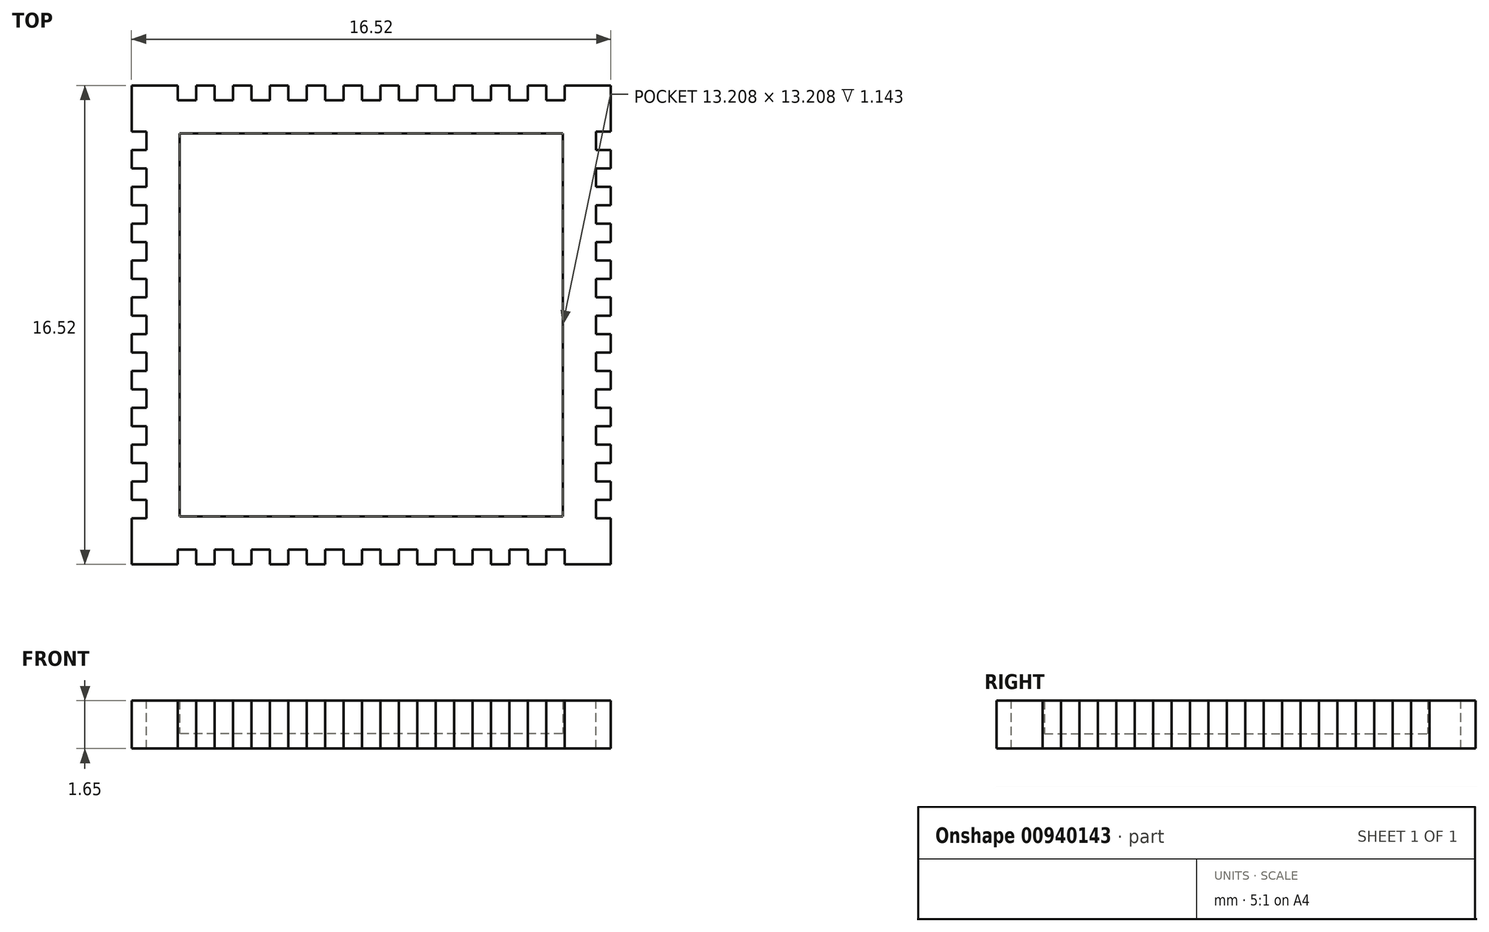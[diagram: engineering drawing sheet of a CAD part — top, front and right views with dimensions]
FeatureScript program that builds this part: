
annotation { "Feature Type Name" : "Feature", "Feature Type Description" : "" }
export const myFeature = defineFeature(function(context is Context, id is Id, definition is map)
    precondition{}
    {
        {
            var Q0;
            Q0=qCreatedBy(makeId("Top.planeOp"),FACE);
            var sketch = newSketch(context, id + "F0", { "sketchPlane" : qUnion([Q0])});
            skLineSegment(sketch, "E0.bottom", {"start": v(8.26, -8.26) * mm, "end": v(-8.26, -8.26) * mm});
            skLineSegment(sketch, "E0.top", {"start": v(8.26, 8.26) * mm, "end": v(-8.26, 8.26) * mm});
            skLineSegment(sketch, "E0.left", {"start": v(8.26, -8.26) * mm, "end": v(8.26, 8.26) * mm});
            skLineSegment(sketch, "E0.right", {"start": v(-8.26, -8.26) * mm, "end": v(-8.26, 8.26) * mm});
            skPoint(sketch, "E0.middle", {"position": v(0, 0) * mm});
            skLineSegment(sketch, "E1.bottom", {"start": v(6.6, -6.6) * mm, "end": v(-6.6, -6.6) * mm});
            skLineSegment(sketch, "E1.top", {"start": v(6.6, 6.6) * mm, "end": v(-6.6, 6.6) * mm});
            skLineSegment(sketch, "E1.left", {"start": v(6.6, -6.6) * mm, "end": v(6.6, 6.6) * mm});
            skLineSegment(sketch, "E1.right", {"start": v(-6.6, -6.6) * mm, "end": v(-6.6, 6.6) * mm});
            skSolve(sketch);
        }
        {
            var Q0;
            Q0=makeQuery(id+"F0.imprint","IMPRINT",FACE,{"disambiguationData":[TD([[makeQuery(id+"F0.imprint","IMPRINT",EDGE,{"derivedFrom":sQuery(id+"F0.wireOp",EDGE,"E1.bottom")}),-1.0]])]});
            extrude(context, id + "F1", {"entities" : qUnion([Q0]), "depth" : 0.5 * mm, "offsetDistance" : 25 * mm});
        }
        {
            var Q0;
            Q0=makeQuery(id+"F0.imprint","IMPRINT",FACE,{"disambiguationData":[TD([[makeQuery(id+"F0.imprint","IMPRINT",EDGE,{"derivedFrom":sQuery(id+"F0.wireOp",EDGE,"E0.bottom")}),-1.0]])]});
            extrude(context, id + "F2", {"entities" : qUnion([Q0]), "operationType" : NewBodyOperationType.ADD, "depth" : 1.65 * mm, "offsetDistance" : 25 * mm});
        }
        {
            var Q0;
            Q0=makeQuery(id+"F2.opExtrude","SWEPT_FACE",FACE,{"disambiguationData":[OSD([sQuery(id+"F0.wireOp",EDGE,"E0.bottom")])]});
            var sketch = newSketch(context, id + "F3", { "sketchPlane" : qUnion([Q0])});
            skLineSegment(sketch, "E2.bottom", {"start": v(-6.03, 0) * mm, "end": v(-6.67, 0) * mm});
            skLineSegment(sketch, "E2.top", {"start": v(-6.03, 1.65) * mm, "end": v(-6.67, 1.65) * mm});
            skLineSegment(sketch, "E2.left", {"start": v(-6.03, 0) * mm, "end": v(-6.03, 1.65) * mm});
            skLineSegment(sketch, "E2.right", {"start": v(-6.67, 0) * mm, "end": v(-6.67, 1.65) * mm});
            skPoint(sketch, "E2.middle", {"position": v(-6.35, 0.83) * mm});
            skLineSegment(sketch, "E3.bottom", {"start": v(-4.76, 0) * mm, "end": v(-5.4, 0) * mm});
            skLineSegment(sketch, "E3.top", {"start": v(-4.76, 1.65) * mm, "end": v(-5.4, 1.65) * mm});
            skLineSegment(sketch, "E3.left", {"start": v(-4.76, 0) * mm, "end": v(-4.76, 1.65) * mm});
            skLineSegment(sketch, "E3.right", {"start": v(-5.4, 0) * mm, "end": v(-5.4, 1.65) * mm});
            skPoint(sketch, "E3.middle", {"position": v(-5.08, 0.83) * mm});
            skLineSegment(sketch, "E4.MirrorCS", {"start": v(-4.13, 0) * mm, "end": v(-3.5, 0) * mm});
            skLineSegment(sketch, "E5.MirrorCS", {"start": v(-4.13, 1.65) * mm, "end": v(-3.5, 1.65) * mm});
            skPoint(sketch, "E6.MirrorP", {"position": v(-2.8, 0.8) * mm});
            skLineSegment(sketch, "E7.MirrorCS", {"start": v(-4.13, 0) * mm, "end": v(-4.13, 1.65) * mm});
            skLineSegment(sketch, "E8.MirrorCS", {"start": v(-2.86, 0) * mm, "end": v(-2.22, 0) * mm});
            skLineSegment(sketch, "E9.MirrorCS", {"start": v(-2.22, 0) * mm, "end": v(-2.22, 1.65) * mm});
            skLineSegment(sketch, "E10.MirrorCS", {"start": v(-2.86, 0) * mm, "end": v(-2.86, 1.65) * mm});
            skPoint(sketch, "E11.MirrorP", {"position": v(-4.1, 0.84) * mm});
            skLineSegment(sketch, "E12.MirrorCS", {"start": v(-3.5, 0) * mm, "end": v(-3.5, 1.65) * mm});
            skLineSegment(sketch, "E13.MirrorCS", {"start": v(-2.86, 1.65) * mm, "end": v(-2.22, 1.65) * mm});
            skLineSegment(sketch, "E14.MirrorCS", {"start": v(0.32, 0) * mm, "end": v(-0.32, 0) * mm});
            skPoint(sketch, "E15.MirrorP", {"position": v(-0.3, 0.84) * mm});
            skLineSegment(sketch, "E16.MirrorCS", {"start": v(-1.59, 0) * mm, "end": v(-1.59, 1.65) * mm});
            skLineSegment(sketch, "E17.MirrorCS", {"start": v(0.95, 0) * mm, "end": v(0.95, 1.65) * mm});
            skLineSegment(sketch, "E18.MirrorCS", {"start": v(-0.32, 0) * mm, "end": v(-0.32, 1.65) * mm});
            skLineSegment(sketch, "E19.MirrorCS", {"start": v(0.32, 0) * mm, "end": v(0.32, 1.65) * mm});
            skPoint(sketch, "E20.MirrorP", {"position": v(-1.56, 0.82) * mm});
            skLineSegment(sketch, "E21.MirrorCS", {"start": v(2.22, 1.65) * mm, "end": v(2.86, 1.65) * mm});
            skLineSegment(sketch, "E22.MirrorCS", {"start": v(2.86, 0) * mm, "end": v(2.86, 1.65) * mm});
            skLineSegment(sketch, "E23.MirrorCS", {"start": v(-0.95, 1.65) * mm, "end": v(-1.59, 1.65) * mm});
            skPoint(sketch, "E24.MirrorP", {"position": v(2.22, 0.83) * mm});
            skLineSegment(sketch, "E25.MirrorCS", {"start": v(-0.95, 0) * mm, "end": v(-1.59, 0) * mm});
            skLineSegment(sketch, "E26.MirrorCS", {"start": v(-0.95, 0) * mm, "end": v(-0.95, 1.65) * mm});
            skLineSegment(sketch, "E27.MirrorCS", {"start": v(0.95, 0) * mm, "end": v(1.59, 0) * mm});
            skLineSegment(sketch, "E28.MirrorCS", {"start": v(0.32, 1.65) * mm, "end": v(-0.32, 1.65) * mm});
            skLineSegment(sketch, "E29.MirrorCS", {"start": v(1.59, 0) * mm, "end": v(1.59, 1.65) * mm});
            skLineSegment(sketch, "E30.MirrorCS", {"start": v(0.95, 1.65) * mm, "end": v(1.59, 1.65) * mm});
            skLineSegment(sketch, "E31.MirrorCS", {"start": v(2.22, 0) * mm, "end": v(2.22, 1.65) * mm});
            skLineSegment(sketch, "E32.MirrorCS", {"start": v(2.22, 0) * mm, "end": v(2.86, 0) * mm});
            skPoint(sketch, "E33.MirrorP", {"position": v(0.95, 0.83) * mm});
            skLineSegment(sketch, "E34.MirrorCS", {"start": v(3.5, 0) * mm, "end": v(3.5, 1.65) * mm});
            skPoint(sketch, "E35.MirrorP", {"position": v(5.96, 0.82) * mm});
            skLineSegment(sketch, "E36.MirrorCS", {"start": v(6.03, 0) * mm, "end": v(6.67, 0) * mm});
            skLineSegment(sketch, "E37.MirrorCS", {"start": v(6.03, 0) * mm, "end": v(6.03, 1.65) * mm});
            skLineSegment(sketch, "E38.MirrorCS", {"start": v(5.4, 1.65) * mm, "end": v(4.76, 1.65) * mm});
            skPoint(sketch, "E39.MirrorP", {"position": v(4.76, 0.83) * mm});
            skLineSegment(sketch, "E40.MirrorCS", {"start": v(6.67, 0) * mm, "end": v(6.67, 1.65) * mm});
            skLineSegment(sketch, "E41.MirrorCS", {"start": v(5.4, 0) * mm, "end": v(5.4, 1.65) * mm});
            skLineSegment(sketch, "E42.MirrorCS", {"start": v(4.13, 0) * mm, "end": v(4.13, 1.65) * mm});
            skLineSegment(sketch, "E43.MirrorCS", {"start": v(4.76, 0) * mm, "end": v(4.76, 1.65) * mm});
            skLineSegment(sketch, "E44.MirrorCS", {"start": v(4.13, 0) * mm, "end": v(3.5, 0) * mm});
            skLineSegment(sketch, "E45.MirrorCS", {"start": v(5.4, 0) * mm, "end": v(4.76, 0) * mm});
            skLineSegment(sketch, "E46.MirrorCS", {"start": v(6.03, 1.65) * mm, "end": v(6.67, 1.65) * mm});
            skPoint(sketch, "E47.MirrorP", {"position": v(3.5, 0.83) * mm});
            skLineSegment(sketch, "E48.MirrorCS", {"start": v(4.13, 1.65) * mm, "end": v(3.5, 1.65) * mm});
            skLineSegment(sketch, "E49", {"start": v(-8.26, 0.83) * mm, "end": v(8.26, 0.83) * mm});
            skSolve(sketch);
        }
        {
            var Q0;
            {var subQ0=sQuery(id+"F3.wireOp",EDGE,"E2.top");Q0=makeQuery(id+"F3.imprint","IMPRINT",FACE,{"disambiguationData":[TD([[makeQuery(id+"F3.imprint","IMPRINT",EDGE,{"derivedFrom":subQ0}),1.0]])]});}
            var Q1;
            {var subQ0=sQuery(id+"F3.wireOp",EDGE,"E2.bottom");Q1=makeQuery(id+"F3.imprint","IMPRINT",FACE,{"disambiguationData":[TD([[makeQuery(id+"F3.imprint","IMPRINT",EDGE,{"derivedFrom":subQ0}),-1.0]])]});}
            var Q2;
            {var subQ0=sQuery(id+"F3.wireOp",EDGE,"E3.top");Q2=makeQuery(id+"F3.imprint","IMPRINT",FACE,{"disambiguationData":[TD([[makeQuery(id+"F3.imprint","IMPRINT",EDGE,{"derivedFrom":subQ0}),1.0]])]});}
            var Q3;
            {var subQ0=sQuery(id+"F3.wireOp",EDGE,"E3.bottom");Q3=makeQuery(id+"F3.imprint","IMPRINT",FACE,{"disambiguationData":[TD([[makeQuery(id+"F3.imprint","IMPRINT",EDGE,{"derivedFrom":subQ0}),-1.0]])]});}
            var Q4;
            {var subQ0=sQuery(id+"F3.wireOp",EDGE,"E5.MirrorCS");Q4=makeQuery(id+"F3.imprint","IMPRINT",FACE,{"disambiguationData":[TD([[makeQuery(id+"F3.imprint","IMPRINT",EDGE,{"derivedFrom":subQ0}),1.0]])]});}
            var Q5;
            {var subQ0=sQuery(id+"F3.wireOp",EDGE,"E4.MirrorCS");Q5=makeQuery(id+"F3.imprint","IMPRINT",FACE,{"disambiguationData":[TD([[makeQuery(id+"F3.imprint","IMPRINT",EDGE,{"derivedFrom":subQ0}),-1.0]])]});}
            var Q6;
            {var subQ0=sQuery(id+"F3.wireOp",EDGE,"E13.MirrorCS");Q6=makeQuery(id+"F3.imprint","IMPRINT",FACE,{"disambiguationData":[TD([[makeQuery(id+"F3.imprint","IMPRINT",EDGE,{"derivedFrom":subQ0}),1.0]])]});}
            var Q7;
            {var subQ0=sQuery(id+"F3.wireOp",EDGE,"E8.MirrorCS");Q7=makeQuery(id+"F3.imprint","IMPRINT",FACE,{"disambiguationData":[TD([[makeQuery(id+"F3.imprint","IMPRINT",EDGE,{"derivedFrom":subQ0}),-1.0]])]});}
            var Q8;
            {var subQ0=sQuery(id+"F3.wireOp",EDGE,"E23.MirrorCS");Q8=makeQuery(id+"F3.imprint","IMPRINT",FACE,{"disambiguationData":[TD([[makeQuery(id+"F3.imprint","IMPRINT",EDGE,{"derivedFrom":subQ0}),1.0]])]});}
            var Q9;
            {var subQ0=sQuery(id+"F3.wireOp",EDGE,"E25.MirrorCS");Q9=makeQuery(id+"F3.imprint","IMPRINT",FACE,{"disambiguationData":[TD([[makeQuery(id+"F3.imprint","IMPRINT",EDGE,{"derivedFrom":subQ0}),-1.0]])]});}
            var Q10;
            {var subQ0=sQuery(id+"F3.wireOp",EDGE,"E28.MirrorCS");Q10=makeQuery(id+"F3.imprint","IMPRINT",FACE,{"disambiguationData":[TD([[makeQuery(id+"F3.imprint","IMPRINT",EDGE,{"derivedFrom":subQ0}),1.0]])]});}
            var Q11;
            {var subQ0=sQuery(id+"F3.wireOp",EDGE,"E14.MirrorCS");Q11=makeQuery(id+"F3.imprint","IMPRINT",FACE,{"disambiguationData":[TD([[makeQuery(id+"F3.imprint","IMPRINT",EDGE,{"derivedFrom":subQ0}),-1.0]])]});}
            var Q12;
            {var subQ0=sQuery(id+"F3.wireOp",EDGE,"E30.MirrorCS");Q12=makeQuery(id+"F3.imprint","IMPRINT",FACE,{"disambiguationData":[TD([[makeQuery(id+"F3.imprint","IMPRINT",EDGE,{"derivedFrom":subQ0}),1.0]])]});}
            var Q13;
            {var subQ0=sQuery(id+"F3.wireOp",EDGE,"E27.MirrorCS");Q13=makeQuery(id+"F3.imprint","IMPRINT",FACE,{"disambiguationData":[TD([[makeQuery(id+"F3.imprint","IMPRINT",EDGE,{"derivedFrom":subQ0}),-1.0]])]});}
            var Q14;
            {var subQ0=sQuery(id+"F3.wireOp",EDGE,"E21.MirrorCS");Q14=makeQuery(id+"F3.imprint","IMPRINT",FACE,{"disambiguationData":[TD([[makeQuery(id+"F3.imprint","IMPRINT",EDGE,{"derivedFrom":subQ0}),1.0]])]});}
            var Q15;
            {var subQ0=sQuery(id+"F3.wireOp",EDGE,"E32.MirrorCS");Q15=makeQuery(id+"F3.imprint","IMPRINT",FACE,{"disambiguationData":[TD([[makeQuery(id+"F3.imprint","IMPRINT",EDGE,{"derivedFrom":subQ0}),-1.0]])]});}
            var Q16;
            {var subQ0=sQuery(id+"F3.wireOp",EDGE,"E48.MirrorCS");Q16=makeQuery(id+"F3.imprint","IMPRINT",FACE,{"disambiguationData":[TD([[makeQuery(id+"F3.imprint","IMPRINT",EDGE,{"derivedFrom":subQ0}),1.0]])]});}
            var Q17;
            {var subQ0=sQuery(id+"F3.wireOp",EDGE,"E44.MirrorCS");Q17=makeQuery(id+"F3.imprint","IMPRINT",FACE,{"disambiguationData":[TD([[makeQuery(id+"F3.imprint","IMPRINT",EDGE,{"derivedFrom":subQ0}),-1.0]])]});}
            var Q18;
            {var subQ0=sQuery(id+"F3.wireOp",EDGE,"E38.MirrorCS");Q18=makeQuery(id+"F3.imprint","IMPRINT",FACE,{"disambiguationData":[TD([[makeQuery(id+"F3.imprint","IMPRINT",EDGE,{"derivedFrom":subQ0}),1.0]])]});}
            var Q19;
            {var subQ0=sQuery(id+"F3.wireOp",EDGE,"E45.MirrorCS");Q19=makeQuery(id+"F3.imprint","IMPRINT",FACE,{"disambiguationData":[TD([[makeQuery(id+"F3.imprint","IMPRINT",EDGE,{"derivedFrom":subQ0}),-1.0]])]});}
            var Q20;
            {var subQ0=sQuery(id+"F3.wireOp",EDGE,"E46.MirrorCS");Q20=makeQuery(id+"F3.imprint","IMPRINT",FACE,{"disambiguationData":[TD([[makeQuery(id+"F3.imprint","IMPRINT",EDGE,{"derivedFrom":subQ0}),1.0]])]});}
            var Q21;
            {var subQ0=sQuery(id+"F3.wireOp",EDGE,"E36.MirrorCS");Q21=makeQuery(id+"F3.imprint","IMPRINT",FACE,{"disambiguationData":[TD([[makeQuery(id+"F3.imprint","IMPRINT",EDGE,{"derivedFrom":subQ0}),-1.0]])]});}
            extrude(context, id + "F4", {"entities" : qUnion([Q0, Q1, Q2, Q3, Q4, Q5, Q6, Q7, Q8, Q9, Q10, Q11, Q12, Q13, Q14, Q15, Q16, Q17, Q18, Q19, Q20, Q21]), "operationType" : NewBodyOperationType.REMOVE, "oppositeDirection" : true, "depth" : 0.5 * mm, "offsetDistance" : 25 * mm});
        }
        {
            var Q0;
            Q0=makeQuery(id+"F2.opExtrude","SWEPT_FACE",FACE,{"disambiguationData":[OSD([sQuery(id+"F0.wireOp",EDGE,"E0.left")])]});
            var sketch = newSketch(context, id + "F5", { "sketchPlane" : qUnion([Q0])});
            skLineSegment(sketch, "E50.bottom", {"start": v(-6.03, 0) * mm, "end": v(-6.67, 0) * mm});
            skLineSegment(sketch, "E50.top", {"start": v(-6.03, 1.65) * mm, "end": v(-6.67, 1.65) * mm});
            skLineSegment(sketch, "E50.left", {"start": v(-6.03, 0) * mm, "end": v(-6.03, 1.65) * mm});
            skLineSegment(sketch, "E50.right", {"start": v(-6.67, 0) * mm, "end": v(-6.67, 1.65) * mm});
            skPoint(sketch, "E50.middle", {"position": v(-6.35, 0.83) * mm});
            skLineSegment(sketch, "E51.bottom", {"start": v(-4.76, 0) * mm, "end": v(-5.4, 0) * mm});
            skLineSegment(sketch, "E51.top", {"start": v(-4.76, 1.65) * mm, "end": v(-5.4, 1.65) * mm});
            skLineSegment(sketch, "E51.left", {"start": v(-4.76, 0) * mm, "end": v(-4.76, 1.65) * mm});
            skLineSegment(sketch, "E51.right", {"start": v(-5.4, 0) * mm, "end": v(-5.4, 1.65) * mm});
            skPoint(sketch, "E51.middle", {"position": v(-5.08, 0.83) * mm});
            skLineSegment(sketch, "E52.MirrorCS", {"start": v(-4.13, 0) * mm, "end": v(-3.5, 0) * mm});
            skLineSegment(sketch, "E53.MirrorCS", {"start": v(-4.13, 1.65) * mm, "end": v(-3.5, 1.65) * mm});
            skPoint(sketch, "E54.MirrorP", {"position": v(-2.58, 0.8) * mm});
            skLineSegment(sketch, "E55.MirrorCS", {"start": v(-4.13, 0) * mm, "end": v(-4.13, 1.65) * mm});
            skLineSegment(sketch, "E56.MirrorCS", {"start": v(-2.86, 0) * mm, "end": v(-2.22, 0) * mm});
            skLineSegment(sketch, "E57.MirrorCS", {"start": v(-2.22, 0) * mm, "end": v(-2.22, 1.65) * mm});
            skLineSegment(sketch, "E58.MirrorCS", {"start": v(-2.86, 0) * mm, "end": v(-2.86, 1.65) * mm});
            skPoint(sketch, "E59.MirrorP", {"position": v(-3.88, 0.84) * mm});
            skLineSegment(sketch, "E60.MirrorCS", {"start": v(-3.5, 0) * mm, "end": v(-3.5, 1.65) * mm});
            skLineSegment(sketch, "E61.MirrorCS", {"start": v(-2.86, 1.65) * mm, "end": v(-2.22, 1.65) * mm});
            skLineSegment(sketch, "E62.MirrorCS", {"start": v(0.32, 0) * mm, "end": v(-0.32, 0) * mm});
            skPoint(sketch, "E63.MirrorP", {"position": v(-0.09, 0.84) * mm});
            skLineSegment(sketch, "E64.MirrorCS", {"start": v(-1.59, 0) * mm, "end": v(-1.59, 1.65) * mm});
            skLineSegment(sketch, "E65.MirrorCS", {"start": v(0.95, 0) * mm, "end": v(0.95, 1.65) * mm});
            skLineSegment(sketch, "E66.MirrorCS", {"start": v(-0.32, 0) * mm, "end": v(-0.32, 1.65) * mm});
            skLineSegment(sketch, "E67.MirrorCS", {"start": v(0.32, 0) * mm, "end": v(0.32, 1.65) * mm});
            skPoint(sketch, "E68.MirrorP", {"position": v(-1.34, 0.82) * mm});
            skLineSegment(sketch, "E69.MirrorCS", {"start": v(2.22, 1.65) * mm, "end": v(2.86, 1.65) * mm});
            skLineSegment(sketch, "E70.MirrorCS", {"start": v(2.86, 0) * mm, "end": v(2.86, 1.65) * mm});
            skLineSegment(sketch, "E71.MirrorCS", {"start": v(-0.95, 1.65) * mm, "end": v(-1.59, 1.65) * mm});
            skPoint(sketch, "E72.MirrorP", {"position": v(2.44, 0.83) * mm});
            skLineSegment(sketch, "E73.MirrorCS", {"start": v(-0.95, 0) * mm, "end": v(-1.59, 0) * mm});
            skLineSegment(sketch, "E74.MirrorCS", {"start": v(-0.95, 0) * mm, "end": v(-0.95, 1.65) * mm});
            skLineSegment(sketch, "E75.MirrorCS", {"start": v(0.95, 0) * mm, "end": v(1.59, 0) * mm});
            skLineSegment(sketch, "E76.MirrorCS", {"start": v(0.32, 1.65) * mm, "end": v(-0.32, 1.65) * mm});
            skLineSegment(sketch, "E77.MirrorCS", {"start": v(1.59, 0) * mm, "end": v(1.59, 1.65) * mm});
            skLineSegment(sketch, "E78.MirrorCS", {"start": v(0.95, 1.65) * mm, "end": v(1.59, 1.65) * mm});
            skLineSegment(sketch, "E79.MirrorCS", {"start": v(2.22, 0) * mm, "end": v(2.22, 1.65) * mm});
            skLineSegment(sketch, "E80.MirrorCS", {"start": v(2.22, 0) * mm, "end": v(2.86, 0) * mm});
            skPoint(sketch, "E81.MirrorP", {"position": v(1.17, 0.83) * mm});
            skLineSegment(sketch, "E82.MirrorCS", {"start": v(3.5, 0) * mm, "end": v(3.5, 1.65) * mm});
            skPoint(sketch, "E83.MirrorP", {"position": v(6.18, 0.82) * mm});
            skLineSegment(sketch, "E84.MirrorCS", {"start": v(6.03, 0) * mm, "end": v(6.67, 0) * mm});
            skLineSegment(sketch, "E85.MirrorCS", {"start": v(6.03, 0) * mm, "end": v(6.03, 1.65) * mm});
            skLineSegment(sketch, "E86.MirrorCS", {"start": v(5.4, 1.65) * mm, "end": v(4.76, 1.65) * mm});
            skPoint(sketch, "E87.MirrorP", {"position": v(4.98, 0.83) * mm});
            skLineSegment(sketch, "E88.MirrorCS", {"start": v(6.67, 0) * mm, "end": v(6.67, 1.65) * mm});
            skLineSegment(sketch, "E89.MirrorCS", {"start": v(5.4, 0) * mm, "end": v(5.4, 1.65) * mm});
            skLineSegment(sketch, "E90.MirrorCS", {"start": v(4.13, 0) * mm, "end": v(4.13, 1.65) * mm});
            skLineSegment(sketch, "E91.MirrorCS", {"start": v(4.76, 0) * mm, "end": v(4.76, 1.65) * mm});
            skLineSegment(sketch, "E92.MirrorCS", {"start": v(4.13, 0) * mm, "end": v(3.5, 0) * mm});
            skLineSegment(sketch, "E93.MirrorCS", {"start": v(5.4, 0) * mm, "end": v(4.76, 0) * mm});
            skLineSegment(sketch, "E94.MirrorCS", {"start": v(6.03, 1.65) * mm, "end": v(6.67, 1.65) * mm});
            skPoint(sketch, "E95.MirrorP", {"position": v(3.71, 0.83) * mm});
            skLineSegment(sketch, "E96.MirrorCS", {"start": v(4.13, 1.65) * mm, "end": v(3.5, 1.65) * mm});
            skLineSegment(sketch, "E97", {"start": v(-8.26, 0.83) * mm, "end": v(8.26, 0.83) * mm});
            skSolve(sketch);
        }
        {
            var Q0;
            {var subQ0=sQuery(id+"F5.wireOp",EDGE,"E51.bottom");Q0=makeQuery(id+"F5.imprint","IMPRINT",FACE,{"disambiguationData":[TD([[makeQuery(id+"F5.imprint","IMPRINT",EDGE,{"derivedFrom":subQ0}),-1.0]])]});}
            var Q1;
            {var subQ0=sQuery(id+"F5.wireOp",EDGE,"E52.MirrorCS");Q1=makeQuery(id+"F5.imprint","IMPRINT",FACE,{"disambiguationData":[TD([[makeQuery(id+"F5.imprint","IMPRINT",EDGE,{"derivedFrom":subQ0}),1.0]])]});}
            var Q2;
            {var subQ0=sQuery(id+"F5.wireOp",EDGE,"E56.MirrorCS");Q2=makeQuery(id+"F5.imprint","IMPRINT",FACE,{"disambiguationData":[TD([[makeQuery(id+"F5.imprint","IMPRINT",EDGE,{"derivedFrom":subQ0}),1.0]])]});}
            var Q3;
            {var subQ0=sQuery(id+"F5.wireOp",EDGE,"E62.MirrorCS");Q3=makeQuery(id+"F5.imprint","IMPRINT",FACE,{"disambiguationData":[TD([[makeQuery(id+"F5.imprint","IMPRINT",EDGE,{"derivedFrom":subQ0}),-1.0]])]});}
            var Q4;
            {var subQ0=sQuery(id+"F5.wireOp",EDGE,"E73.MirrorCS");Q4=makeQuery(id+"F5.imprint","IMPRINT",FACE,{"disambiguationData":[TD([[makeQuery(id+"F5.imprint","IMPRINT",EDGE,{"derivedFrom":subQ0}),-1.0]])]});}
            var Q5;
            {var subQ0=sQuery(id+"F5.wireOp",EDGE,"E75.MirrorCS");Q5=makeQuery(id+"F5.imprint","IMPRINT",FACE,{"disambiguationData":[TD([[makeQuery(id+"F5.imprint","IMPRINT",EDGE,{"derivedFrom":subQ0}),1.0]])]});}
            var Q6;
            {var subQ0=sQuery(id+"F5.wireOp",EDGE,"E80.MirrorCS");Q6=makeQuery(id+"F5.imprint","IMPRINT",FACE,{"disambiguationData":[TD([[makeQuery(id+"F5.imprint","IMPRINT",EDGE,{"derivedFrom":subQ0}),1.0]])]});}
            var Q7;
            {var subQ0=sQuery(id+"F5.wireOp",EDGE,"E92.MirrorCS");Q7=makeQuery(id+"F5.imprint","IMPRINT",FACE,{"disambiguationData":[TD([[makeQuery(id+"F5.imprint","IMPRINT",EDGE,{"derivedFrom":subQ0}),-1.0]])]});}
            var Q8;
            {var subQ0=sQuery(id+"F5.wireOp",EDGE,"E84.MirrorCS");Q8=makeQuery(id+"F5.imprint","IMPRINT",FACE,{"disambiguationData":[TD([[makeQuery(id+"F5.imprint","IMPRINT",EDGE,{"derivedFrom":subQ0}),1.0]])]});}
            var Q9;
            {var subQ0=sQuery(id+"F5.wireOp",EDGE,"E93.MirrorCS");Q9=makeQuery(id+"F5.imprint","IMPRINT",FACE,{"disambiguationData":[TD([[makeQuery(id+"F5.imprint","IMPRINT",EDGE,{"derivedFrom":subQ0}),-1.0]])]});}
            var Q10;
            {var subQ0=sQuery(id+"F5.wireOp",EDGE,"E50.top");Q10=makeQuery(id+"F5.imprint","IMPRINT",FACE,{"disambiguationData":[TD([[makeQuery(id+"F5.imprint","IMPRINT",EDGE,{"derivedFrom":subQ0}),1.0]])]});}
            var Q11;
            {var subQ0=sQuery(id+"F5.wireOp",EDGE,"E51.top");Q11=makeQuery(id+"F5.imprint","IMPRINT",FACE,{"disambiguationData":[TD([[makeQuery(id+"F5.imprint","IMPRINT",EDGE,{"derivedFrom":subQ0}),1.0]])]});}
            var Q12;
            {var subQ0=sQuery(id+"F5.wireOp",EDGE,"E53.MirrorCS");Q12=makeQuery(id+"F5.imprint","IMPRINT",FACE,{"disambiguationData":[TD([[makeQuery(id+"F5.imprint","IMPRINT",EDGE,{"derivedFrom":subQ0}),-1.0]])]});}
            var Q13;
            {var subQ0=sQuery(id+"F5.wireOp",EDGE,"E61.MirrorCS");Q13=makeQuery(id+"F5.imprint","IMPRINT",FACE,{"disambiguationData":[TD([[makeQuery(id+"F5.imprint","IMPRINT",EDGE,{"derivedFrom":subQ0}),-1.0]])]});}
            var Q14;
            {var subQ0=sQuery(id+"F5.wireOp",EDGE,"E71.MirrorCS");Q14=makeQuery(id+"F5.imprint","IMPRINT",FACE,{"disambiguationData":[TD([[makeQuery(id+"F5.imprint","IMPRINT",EDGE,{"derivedFrom":subQ0}),1.0]])]});}
            var Q15;
            {var subQ0=sQuery(id+"F5.wireOp",EDGE,"E78.MirrorCS");Q15=makeQuery(id+"F5.imprint","IMPRINT",FACE,{"disambiguationData":[TD([[makeQuery(id+"F5.imprint","IMPRINT",EDGE,{"derivedFrom":subQ0}),-1.0]])]});}
            var Q16;
            {var subQ0=sQuery(id+"F5.wireOp",EDGE,"E76.MirrorCS");Q16=makeQuery(id+"F5.imprint","IMPRINT",FACE,{"disambiguationData":[TD([[makeQuery(id+"F5.imprint","IMPRINT",EDGE,{"derivedFrom":subQ0}),1.0]])]});}
            var Q17;
            {var subQ0=sQuery(id+"F5.wireOp",EDGE,"E69.MirrorCS");Q17=makeQuery(id+"F5.imprint","IMPRINT",FACE,{"disambiguationData":[TD([[makeQuery(id+"F5.imprint","IMPRINT",EDGE,{"derivedFrom":subQ0}),-1.0]])]});}
            var Q18;
            {var subQ0=sQuery(id+"F5.wireOp",EDGE,"E96.MirrorCS");Q18=makeQuery(id+"F5.imprint","IMPRINT",FACE,{"disambiguationData":[TD([[makeQuery(id+"F5.imprint","IMPRINT",EDGE,{"derivedFrom":subQ0}),1.0]])]});}
            var Q19;
            {var subQ0=sQuery(id+"F5.wireOp",EDGE,"E94.MirrorCS");Q19=makeQuery(id+"F5.imprint","IMPRINT",FACE,{"disambiguationData":[TD([[makeQuery(id+"F5.imprint","IMPRINT",EDGE,{"derivedFrom":subQ0}),-1.0]])]});}
            var Q20;
            {var subQ0=sQuery(id+"F5.wireOp",EDGE,"E86.MirrorCS");Q20=makeQuery(id+"F5.imprint","IMPRINT",FACE,{"disambiguationData":[TD([[makeQuery(id+"F5.imprint","IMPRINT",EDGE,{"derivedFrom":subQ0}),1.0]])]});}
            var Q21;
            {var subQ0=sQuery(id+"F5.wireOp",EDGE,"E97");var subQ1=sQuery(id+"F5.wireOp",EDGE,"E51.left");var subQ2=makeQuery(id+"F5.imprint","INTERSECT",VERTEX,{"derivedFrom":[subQ1,subQ0]});Q21=makeQuery(id+"F5.imprint","IMPRINT",FACE,{"disambiguationData":[TD([[makeQuery(id+"F5.imprint","IMPRINT",EDGE,{"disambiguationData":[TD([[subQ2,-1.0]])],"derivedFrom":subQ1}),1.0]])]});}
            var Q22;
            {var subQ0=sQuery(id+"F5.wireOp",EDGE,"E97");var subQ1=sQuery(id+"F5.wireOp",EDGE,"E55.MirrorCS");var subQ2=makeQuery(id+"F5.imprint","INTERSECT",VERTEX,{"derivedFrom":[subQ1,subQ0]});Q22=makeQuery(id+"F5.imprint","IMPRINT",FACE,{"disambiguationData":[TD([[makeQuery(id+"F5.imprint","IMPRINT",EDGE,{"disambiguationData":[TD([[subQ2,-1.0]])],"derivedFrom":subQ1}),-1.0]])]});}
            var Q23;
            {var subQ0=sQuery(id+"F5.wireOp",EDGE,"E97");var subQ1=sQuery(id+"F5.wireOp",EDGE,"E57.MirrorCS");var subQ2=makeQuery(id+"F5.imprint","INTERSECT",VERTEX,{"derivedFrom":[subQ1,subQ0]});Q23=makeQuery(id+"F5.imprint","IMPRINT",FACE,{"disambiguationData":[TD([[makeQuery(id+"F5.imprint","IMPRINT",EDGE,{"disambiguationData":[TD([[subQ2,-1.0]])],"derivedFrom":subQ1}),1.0]])]});}
            var Q24;
            {var subQ0=sQuery(id+"F5.wireOp",EDGE,"E97");var subQ1=sQuery(id+"F5.wireOp",EDGE,"E64.MirrorCS");var subQ2=makeQuery(id+"F5.imprint","INTERSECT",VERTEX,{"derivedFrom":[subQ1,subQ0]});Q24=makeQuery(id+"F5.imprint","IMPRINT",FACE,{"disambiguationData":[TD([[makeQuery(id+"F5.imprint","IMPRINT",EDGE,{"disambiguationData":[TD([[subQ2,-1.0]])],"derivedFrom":subQ1}),-1.0]])]});}
            var Q25;
            {var subQ0=sQuery(id+"F5.wireOp",EDGE,"E97");var subQ1=sQuery(id+"F5.wireOp",EDGE,"E65.MirrorCS");var subQ2=makeQuery(id+"F5.imprint","INTERSECT",VERTEX,{"derivedFrom":[subQ1,subQ0]});Q25=makeQuery(id+"F5.imprint","IMPRINT",FACE,{"disambiguationData":[TD([[makeQuery(id+"F5.imprint","IMPRINT",EDGE,{"disambiguationData":[TD([[subQ2,-1.0]])],"derivedFrom":subQ1}),-1.0]])]});}
            var Q26;
            {var subQ0=sQuery(id+"F5.wireOp",EDGE,"E97");var subQ1=sQuery(id+"F5.wireOp",EDGE,"E66.MirrorCS");var subQ2=makeQuery(id+"F5.imprint","INTERSECT",VERTEX,{"derivedFrom":[subQ1,subQ0]});Q26=makeQuery(id+"F5.imprint","IMPRINT",FACE,{"disambiguationData":[TD([[makeQuery(id+"F5.imprint","IMPRINT",EDGE,{"disambiguationData":[TD([[subQ2,-1.0]])],"derivedFrom":subQ1}),-1.0]])]});}
            var Q27;
            {var subQ0=sQuery(id+"F5.wireOp",EDGE,"E97");var subQ1=sQuery(id+"F5.wireOp",EDGE,"E70.MirrorCS");var subQ2=makeQuery(id+"F5.imprint","INTERSECT",VERTEX,{"derivedFrom":[subQ1,subQ0]});Q27=makeQuery(id+"F5.imprint","IMPRINT",FACE,{"disambiguationData":[TD([[makeQuery(id+"F5.imprint","IMPRINT",EDGE,{"disambiguationData":[TD([[subQ2,-1.0]])],"derivedFrom":subQ1}),1.0]])]});}
            var Q28;
            {var subQ0=sQuery(id+"F5.wireOp",EDGE,"E97");var subQ1=sQuery(id+"F5.wireOp",EDGE,"E82.MirrorCS");var subQ2=makeQuery(id+"F5.imprint","INTERSECT",VERTEX,{"derivedFrom":[subQ1,subQ0]});Q28=makeQuery(id+"F5.imprint","IMPRINT",FACE,{"disambiguationData":[TD([[makeQuery(id+"F5.imprint","IMPRINT",EDGE,{"disambiguationData":[TD([[subQ2,-1.0]])],"derivedFrom":subQ1}),-1.0]])]});}
            var Q29;
            {var subQ0=sQuery(id+"F5.wireOp",EDGE,"E97");var subQ1=sQuery(id+"F5.wireOp",EDGE,"E85.MirrorCS");var subQ2=makeQuery(id+"F5.imprint","INTERSECT",VERTEX,{"derivedFrom":[subQ1,subQ0]});Q29=makeQuery(id+"F5.imprint","IMPRINT",FACE,{"disambiguationData":[TD([[makeQuery(id+"F5.imprint","IMPRINT",EDGE,{"disambiguationData":[TD([[subQ2,-1.0]])],"derivedFrom":subQ1}),-1.0]])]});}
            var Q30;
            {var subQ0=sQuery(id+"F5.wireOp",EDGE,"E97");var subQ1=sQuery(id+"F5.wireOp",EDGE,"E89.MirrorCS");var subQ2=makeQuery(id+"F5.imprint","INTERSECT",VERTEX,{"derivedFrom":[subQ1,subQ0]});Q30=makeQuery(id+"F5.imprint","IMPRINT",FACE,{"disambiguationData":[TD([[makeQuery(id+"F5.imprint","IMPRINT",EDGE,{"disambiguationData":[TD([[subQ2,-1.0]])],"derivedFrom":subQ1}),1.0]])]});}
            var Q31;
            {var subQ0=sQuery(id+"F5.wireOp",EDGE,"E97");var subQ1=sQuery(id+"F5.wireOp",EDGE,"E50.left");var subQ2=makeQuery(id+"F5.imprint","INTERSECT",VERTEX,{"derivedFrom":[subQ1,subQ0]});Q31=makeQuery(id+"F5.imprint","IMPRINT",FACE,{"disambiguationData":[TD([[makeQuery(id+"F5.imprint","IMPRINT",EDGE,{"disambiguationData":[TD([[subQ2,-1.0]])],"derivedFrom":subQ1}),1.0]])]});}
            var Q32;
            {var subQ0=sQuery(id+"F5.wireOp",EDGE,"E50.bottom");Q32=makeQuery(id+"F5.imprint","IMPRINT",FACE,{"disambiguationData":[TD([[makeQuery(id+"F5.imprint","IMPRINT",EDGE,{"derivedFrom":subQ0}),-1.0]])]});}
            extrude(context, id + "F6", {"entities" : qUnion([Q0, Q1, Q2, Q3, Q4, Q5, Q6, Q7, Q8, Q9, Q10, Q11, Q12, Q13, Q14, Q15, Q16, Q17, Q18, Q19, Q20, Q21, Q22, Q23, Q24, Q25, Q26, Q27, Q28, Q29, Q30, Q31, Q32]), "operationType" : NewBodyOperationType.REMOVE, "oppositeDirection" : true, "depth" : 0.5 * mm, "offsetDistance" : 25 * mm});
        }
        {
            var Q0;
            Q0=makeQuery(id+"F2.opExtrude","SWEPT_FACE",FACE,{"disambiguationData":[OSD([sQuery(id+"F0.wireOp",EDGE,"E0.top")])]});
            var sketch = newSketch(context, id + "F7", { "sketchPlane" : qUnion([Q0])});
            skLineSegment(sketch, "E98.bottom", {"start": v(-6.03, 0) * mm, "end": v(-6.67, 0) * mm});
            skLineSegment(sketch, "E98.top", {"start": v(-6.03, 1.65) * mm, "end": v(-6.67, 1.65) * mm});
            skLineSegment(sketch, "E98.left", {"start": v(-6.03, 0) * mm, "end": v(-6.03, 1.65) * mm});
            skLineSegment(sketch, "E98.right", {"start": v(-6.67, 0) * mm, "end": v(-6.67, 1.65) * mm});
            skPoint(sketch, "E98.middle", {"position": v(-6.35, 0.83) * mm});
            skLineSegment(sketch, "E99.bottom", {"start": v(-4.76, 0) * mm, "end": v(-5.4, 0) * mm});
            skLineSegment(sketch, "E99.top", {"start": v(-4.76, 1.65) * mm, "end": v(-5.4, 1.65) * mm});
            skLineSegment(sketch, "E99.left", {"start": v(-4.76, 0) * mm, "end": v(-4.76, 1.65) * mm});
            skLineSegment(sketch, "E99.right", {"start": v(-5.4, 0) * mm, "end": v(-5.4, 1.65) * mm});
            skPoint(sketch, "E99.middle", {"position": v(-5.08, 0.83) * mm});
            skLineSegment(sketch, "E100.MirrorCS", {"start": v(-4.13, 0) * mm, "end": v(-3.5, 0) * mm});
            skLineSegment(sketch, "E101.MirrorCS", {"start": v(-4.13, 1.65) * mm, "end": v(-3.5, 1.65) * mm});
            skPoint(sketch, "E102.MirrorP", {"position": v(-2.8, 0.8) * mm});
            skLineSegment(sketch, "E103.MirrorCS", {"start": v(-4.13, 0) * mm, "end": v(-4.13, 1.65) * mm});
            skLineSegment(sketch, "E104.MirrorCS", {"start": v(-2.86, 0) * mm, "end": v(-2.22, 0) * mm});
            skLineSegment(sketch, "E105.MirrorCS", {"start": v(-2.22, 0) * mm, "end": v(-2.22, 1.65) * mm});
            skLineSegment(sketch, "E106.MirrorCS", {"start": v(-2.86, 0) * mm, "end": v(-2.86, 1.65) * mm});
            skPoint(sketch, "E107.MirrorP", {"position": v(-4.1, 0.84) * mm});
            skLineSegment(sketch, "E108.MirrorCS", {"start": v(-3.5, 0) * mm, "end": v(-3.5, 1.65) * mm});
            skLineSegment(sketch, "E109.MirrorCS", {"start": v(-2.86, 1.65) * mm, "end": v(-2.22, 1.65) * mm});
            skLineSegment(sketch, "E110.MirrorCS", {"start": v(0.32, 0) * mm, "end": v(-0.32, 0) * mm});
            skPoint(sketch, "E111.MirrorP", {"position": v(-0.3, 0.84) * mm});
            skLineSegment(sketch, "E112.MirrorCS", {"start": v(-1.59, 0) * mm, "end": v(-1.59, 1.65) * mm});
            skLineSegment(sketch, "E113.MirrorCS", {"start": v(0.95, 0) * mm, "end": v(0.95, 1.65) * mm});
            skLineSegment(sketch, "E114.MirrorCS", {"start": v(-0.32, 0) * mm, "end": v(-0.32, 1.65) * mm});
            skLineSegment(sketch, "E115.MirrorCS", {"start": v(0.32, 0) * mm, "end": v(0.32, 1.65) * mm});
            skPoint(sketch, "E116.MirrorP", {"position": v(-1.56, 0.82) * mm});
            skLineSegment(sketch, "E117.MirrorCS", {"start": v(2.22, 1.65) * mm, "end": v(2.86, 1.65) * mm});
            skLineSegment(sketch, "E118.MirrorCS", {"start": v(2.86, 0) * mm, "end": v(2.86, 1.65) * mm});
            skLineSegment(sketch, "E119.MirrorCS", {"start": v(-0.95, 1.65) * mm, "end": v(-1.59, 1.65) * mm});
            skPoint(sketch, "E120.MirrorP", {"position": v(2.22, 0.83) * mm});
            skLineSegment(sketch, "E121.MirrorCS", {"start": v(-0.95, 0) * mm, "end": v(-1.59, 0) * mm});
            skLineSegment(sketch, "E122.MirrorCS", {"start": v(-0.95, 0) * mm, "end": v(-0.95, 1.65) * mm});
            skLineSegment(sketch, "E123.MirrorCS", {"start": v(0.95, 0) * mm, "end": v(1.59, 0) * mm});
            skLineSegment(sketch, "E124.MirrorCS", {"start": v(0.32, 1.65) * mm, "end": v(-0.32, 1.65) * mm});
            skLineSegment(sketch, "E125.MirrorCS", {"start": v(1.59, 0) * mm, "end": v(1.59, 1.65) * mm});
            skLineSegment(sketch, "E126.MirrorCS", {"start": v(0.95, 1.65) * mm, "end": v(1.59, 1.65) * mm});
            skLineSegment(sketch, "E127.MirrorCS", {"start": v(2.22, 0) * mm, "end": v(2.22, 1.65) * mm});
            skLineSegment(sketch, "E128.MirrorCS", {"start": v(2.22, 0) * mm, "end": v(2.86, 0) * mm});
            skPoint(sketch, "E129.MirrorP", {"position": v(0.95, 0.83) * mm});
            skLineSegment(sketch, "E130.MirrorCS", {"start": v(3.5, 0) * mm, "end": v(3.5, 1.65) * mm});
            skPoint(sketch, "E131.MirrorP", {"position": v(5.96, 0.82) * mm});
            skLineSegment(sketch, "E132.MirrorCS", {"start": v(6.03, 0) * mm, "end": v(6.67, 0) * mm});
            skLineSegment(sketch, "E133.MirrorCS", {"start": v(6.03, 0) * mm, "end": v(6.03, 1.65) * mm});
            skLineSegment(sketch, "E134.MirrorCS", {"start": v(5.4, 1.65) * mm, "end": v(4.76, 1.65) * mm});
            skPoint(sketch, "E135.MirrorP", {"position": v(4.76, 0.83) * mm});
            skLineSegment(sketch, "E136.MirrorCS", {"start": v(6.67, 0) * mm, "end": v(6.67, 1.65) * mm});
            skLineSegment(sketch, "E137.MirrorCS", {"start": v(5.4, 0) * mm, "end": v(5.4, 1.65) * mm});
            skLineSegment(sketch, "E138.MirrorCS", {"start": v(4.13, 0) * mm, "end": v(4.13, 1.65) * mm});
            skLineSegment(sketch, "E139.MirrorCS", {"start": v(4.76, 0) * mm, "end": v(4.76, 1.65) * mm});
            skLineSegment(sketch, "E140.MirrorCS", {"start": v(4.13, 0) * mm, "end": v(3.5, 0) * mm});
            skLineSegment(sketch, "E141.MirrorCS", {"start": v(5.4, 0) * mm, "end": v(4.76, 0) * mm});
            skLineSegment(sketch, "E142.MirrorCS", {"start": v(6.03, 1.65) * mm, "end": v(6.67, 1.65) * mm});
            skPoint(sketch, "E143.MirrorP", {"position": v(3.5, 0.83) * mm});
            skLineSegment(sketch, "E144.MirrorCS", {"start": v(4.13, 1.65) * mm, "end": v(3.5, 1.65) * mm});
            skLineSegment(sketch, "E145", {"start": v(-8.26, 0.83) * mm, "end": v(8.26, 0.83) * mm});
            skSolve(sketch);
        }
        {
            var Q0;
            Q0 = qSketchRegion(id + "F7", true);
            extrude(context, id + "F8", {"entities" : qUnion([Q0]), "operationType" : NewBodyOperationType.REMOVE, "oppositeDirection" : true, "depth" : 0.5 * mm, "offsetDistance" : 25 * mm});
        }
        {
            var Q0;
            Q0=makeQuery(id+"F2.opExtrude","SWEPT_FACE",FACE,{"disambiguationData":[OSD([sQuery(id+"F0.wireOp",EDGE,"E0.right")])]});
            var sketch = newSketch(context, id + "F9", { "sketchPlane" : qUnion([Q0])});
            skLineSegment(sketch, "E146.bottom", {"start": v(-6.03, 0) * mm, "end": v(-6.67, 0) * mm});
            skLineSegment(sketch, "E146.top", {"start": v(-6.03, 1.65) * mm, "end": v(-6.67, 1.65) * mm});
            skLineSegment(sketch, "E146.left", {"start": v(-6.03, 0) * mm, "end": v(-6.03, 1.65) * mm});
            skLineSegment(sketch, "E146.right", {"start": v(-6.67, 0) * mm, "end": v(-6.67, 1.65) * mm});
            skPoint(sketch, "E146.middle", {"position": v(-6.35, 0.82) * mm});
            skLineSegment(sketch, "E147.bottom", {"start": v(-4.76, 0) * mm, "end": v(-5.4, 0) * mm});
            skLineSegment(sketch, "E147.top", {"start": v(-4.76, 1.65) * mm, "end": v(-5.4, 1.65) * mm});
            skLineSegment(sketch, "E147.left", {"start": v(-4.76, 0) * mm, "end": v(-4.76, 1.65) * mm});
            skLineSegment(sketch, "E147.right", {"start": v(-5.4, 0) * mm, "end": v(-5.4, 1.65) * mm});
            skPoint(sketch, "E147.middle", {"position": v(-5.08, 0.82) * mm});
            skLineSegment(sketch, "E148.MirrorCS", {"start": v(-4.13, 0) * mm, "end": v(-3.5, 0) * mm});
            skLineSegment(sketch, "E149.MirrorCS", {"start": v(-4.13, 1.65) * mm, "end": v(-3.5, 1.65) * mm});
            skPoint(sketch, "E150.MirrorP", {"position": v(-2.8, 0.8) * mm});
            skLineSegment(sketch, "E151.MirrorCS", {"start": v(-4.13, 0) * mm, "end": v(-4.13, 1.65) * mm});
            skLineSegment(sketch, "E152.MirrorCS", {"start": v(-2.86, 0) * mm, "end": v(-2.22, 0) * mm});
            skLineSegment(sketch, "E153.MirrorCS", {"start": v(-2.22, 0) * mm, "end": v(-2.22, 1.65) * mm});
            skLineSegment(sketch, "E154.MirrorCS", {"start": v(-2.86, 0) * mm, "end": v(-2.86, 1.65) * mm});
            skPoint(sketch, "E155.MirrorP", {"position": v(-4.1, 0.84) * mm});
            skLineSegment(sketch, "E156.MirrorCS", {"start": v(-3.5, 0) * mm, "end": v(-3.5, 1.65) * mm});
            skLineSegment(sketch, "E157.MirrorCS", {"start": v(-2.86, 1.65) * mm, "end": v(-2.22, 1.65) * mm});
            skLineSegment(sketch, "E158.MirrorCS", {"start": v(0.32, 0) * mm, "end": v(-0.32, 0) * mm});
            skPoint(sketch, "E159.MirrorP", {"position": v(-0.3, 0.84) * mm});
            skLineSegment(sketch, "E160.MirrorCS", {"start": v(-1.59, 0) * mm, "end": v(-1.59, 1.65) * mm});
            skLineSegment(sketch, "E161.MirrorCS", {"start": v(0.95, 0) * mm, "end": v(0.95, 1.65) * mm});
            skLineSegment(sketch, "E162.MirrorCS", {"start": v(-0.32, 0) * mm, "end": v(-0.32, 1.65) * mm});
            skLineSegment(sketch, "E163.MirrorCS", {"start": v(0.32, 0) * mm, "end": v(0.32, 1.65) * mm});
            skPoint(sketch, "E164.MirrorP", {"position": v(-1.56, 0.81) * mm});
            skLineSegment(sketch, "E165.MirrorCS", {"start": v(2.22, 1.65) * mm, "end": v(2.86, 1.65) * mm});
            skLineSegment(sketch, "E166.MirrorCS", {"start": v(2.86, 0) * mm, "end": v(2.86, 1.65) * mm});
            skLineSegment(sketch, "E167.MirrorCS", {"start": v(-0.95, 1.65) * mm, "end": v(-1.59, 1.65) * mm});
            skPoint(sketch, "E168.MirrorP", {"position": v(2.22, 0.82) * mm});
            skLineSegment(sketch, "E169.MirrorCS", {"start": v(-0.95, 0) * mm, "end": v(-1.59, 0) * mm});
            skLineSegment(sketch, "E170.MirrorCS", {"start": v(-0.95, 0) * mm, "end": v(-0.95, 1.65) * mm});
            skLineSegment(sketch, "E171.MirrorCS", {"start": v(0.95, 0) * mm, "end": v(1.59, 0) * mm});
            skLineSegment(sketch, "E172.MirrorCS", {"start": v(0.32, 1.65) * mm, "end": v(-0.32, 1.65) * mm});
            skLineSegment(sketch, "E173.MirrorCS", {"start": v(1.59, 0) * mm, "end": v(1.59, 1.65) * mm});
            skLineSegment(sketch, "E174.MirrorCS", {"start": v(0.95, 1.65) * mm, "end": v(1.59, 1.65) * mm});
            skLineSegment(sketch, "E175.MirrorCS", {"start": v(2.22, 0) * mm, "end": v(2.22, 1.65) * mm});
            skLineSegment(sketch, "E176.MirrorCS", {"start": v(2.22, 0) * mm, "end": v(2.86, 0) * mm});
            skPoint(sketch, "E177.MirrorP", {"position": v(0.95, 0.82) * mm});
            skLineSegment(sketch, "E178.MirrorCS", {"start": v(3.5, 0) * mm, "end": v(3.5, 1.65) * mm});
            skPoint(sketch, "E179.MirrorP", {"position": v(5.96, 0.81) * mm});
            skLineSegment(sketch, "E180.MirrorCS", {"start": v(6.03, 0) * mm, "end": v(6.67, 0) * mm});
            skLineSegment(sketch, "E181.MirrorCS", {"start": v(6.03, 0) * mm, "end": v(6.03, 1.65) * mm});
            skLineSegment(sketch, "E182.MirrorCS", {"start": v(5.4, 1.65) * mm, "end": v(4.76, 1.65) * mm});
            skPoint(sketch, "E183.MirrorP", {"position": v(4.76, 0.82) * mm});
            skLineSegment(sketch, "E184.MirrorCS", {"start": v(6.67, 0) * mm, "end": v(6.67, 1.65) * mm});
            skLineSegment(sketch, "E185.MirrorCS", {"start": v(5.4, 0) * mm, "end": v(5.4, 1.65) * mm});
            skLineSegment(sketch, "E186.MirrorCS", {"start": v(4.13, 0) * mm, "end": v(4.13, 1.65) * mm});
            skLineSegment(sketch, "E187.MirrorCS", {"start": v(4.76, 0) * mm, "end": v(4.76, 1.65) * mm});
            skLineSegment(sketch, "E188.MirrorCS", {"start": v(4.13, 0) * mm, "end": v(3.5, 0) * mm});
            skLineSegment(sketch, "E189.MirrorCS", {"start": v(5.4, 0) * mm, "end": v(4.76, 0) * mm});
            skLineSegment(sketch, "E190.MirrorCS", {"start": v(6.03, 1.65) * mm, "end": v(6.67, 1.65) * mm});
            skPoint(sketch, "E191.MirrorP", {"position": v(3.5, 0.82) * mm});
            skLineSegment(sketch, "E192.MirrorCS", {"start": v(4.13, 1.65) * mm, "end": v(3.5, 1.65) * mm});
            skLineSegment(sketch, "E193", {"start": v(-8.26, 0.82) * mm, "end": v(8.25, 0.82) * mm});
            skSolve(sketch);
        }
        {
            var Q0;
            Q0 = qSketchRegion(id + "F9", true);
            extrude(context, id + "F10", {"entities" : qUnion([Q0]), "operationType" : NewBodyOperationType.REMOVE, "oppositeDirection" : true, "depth" : 0.5 * mm, "offsetDistance" : 25 * mm});
        }
    });
